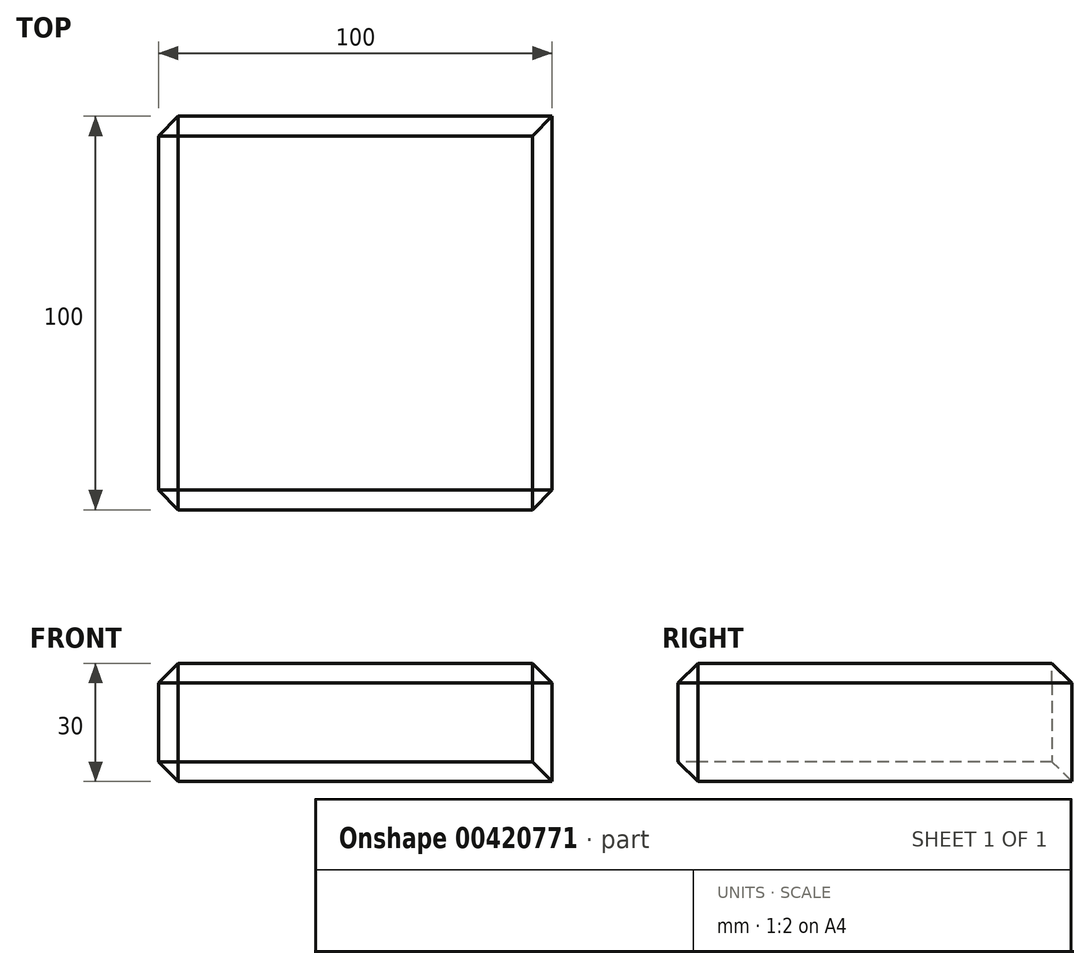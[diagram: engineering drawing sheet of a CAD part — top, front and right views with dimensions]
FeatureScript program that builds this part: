
annotation { "Feature Type Name" : "Feature", "Feature Type Description" : "" }
export const myFeature = defineFeature(function(context is Context, id is Id, definition is map)
    precondition{}
    {
        {
            var Q0;
            Q0=qCreatedBy(makeId("Top.planeOp"),FACE);
            var sketch = newSketch(context, id + "F0", { "sketchPlane" : qUnion([Q0])});
            skLineSegment(sketch, "E0.bottom", {"start": v(-34.16, 60.12) * mm, "end": v(65.84, 60.12) * mm});
            skLineSegment(sketch, "E0.top", {"start": v(-34.16, -39.88) * mm, "end": v(65.84, -39.88) * mm});
            skLineSegment(sketch, "E0.left", {"start": v(-34.16, 60.12) * mm, "end": v(-34.16, -39.88) * mm});
            skLineSegment(sketch, "E0.right", {"start": v(65.84, 60.12) * mm, "end": v(65.84, -39.88) * mm});
            skSolve(sketch);
        }
        {
            var Q0;
            Q0=makeQuery(id+"F0.imprint","IMPRINT",FACE,{"disambiguationData":[TD([[makeQuery(id+"F0.imprint","IMPRINT",EDGE,{"derivedFrom":sQuery(id+"F0.wireOp",EDGE,"E0.bottom")}),-1.0]])]});
            extrude(context, id + "F1", {"entities" : qUnion([Q0]), "depth" : 30 * mm});
        }
        {
            var Q0;
            Q0=makeQuery(id+"F1.opExtrude","CAP_FACE",FACE,{"disambiguationData":[OSD([sQuery(id+"F0.wireOp",EDGE,"E0.bottom"),sQuery(id+"F0.wireOp",EDGE,"E0.top"),sQuery(id+"F0.wireOp",EDGE,"E0.left"),sQuery(id+"F0.wireOp",EDGE,"E0.right")])],"isStart":false});
            var sketch = newSketch(context, id + "F2", { "sketchPlane" : qUnion([Q0])});
            skCircle(sketch, "E1", {"center": v(11.84, 16.56) * mm, "radius": 15 * mm});
            skSolve(sketch);
        }
        {
            var Q0;
            Q0=makeQuery(id+"F2.imprint","IMPRINT",FACE,{"disambiguationData":[TD([[makeQuery(id+"F2.imprint","IMPRINT",EDGE,{"derivedFrom":sQuery(id+"F2.wireOp",EDGE,"E1")}),-1.0]])]});
            var Q1;
            Q1=makeQuery(id+"F2.imprint","IMPRINT",FACE,{"disambiguationData":[TD([[makeQuery(id+"F2.imprint","IMPRINT",EDGE,{"derivedFrom":sQuery(id+"F2.wireOp",EDGE,"E1")}),1.0]])]});
            var Q2;
            Q2=sQuery(id+"F2.wireOp",EDGE,"E1");
            extrude(context, id + "F3", {"entities" : qUnion([Q0, Q1]), "bodyType" : ToolBodyType.SURFACE, "operationType" : NewBodyOperationType.ADD, "surfaceEntities" : qUnion([Q2]), "depth" : 40 * mm});
        }
        {
            var Q0;
            Q0=makeQuery(id+"F1.opExtrude","CAP_FACE",FACE,{"disambiguationData":[OSD([sQuery(id+"F0.wireOp",EDGE,"E0.bottom"),sQuery(id+"F0.wireOp",EDGE,"E0.top"),sQuery(id+"F0.wireOp",EDGE,"E0.left"),sQuery(id+"F0.wireOp",EDGE,"E0.right")])],"isStart":false});
            var Q1;
            Q1=makeQuery(id+"F1.opExtrude","SWEPT_FACE",FACE,{"disambiguationData":[OSD([sQuery(id+"F0.wireOp",EDGE,"E0.top")])]});
            var Q2;
            Q2=makeQuery(id+"F1.opExtrude","SWEPT_FACE",FACE,{"disambiguationData":[OSD([sQuery(id+"F0.wireOp",EDGE,"E0.left")])]});
            chamfer(context, id + "F4", {"entities" : qUnion([Q0, Q1, Q2]), "width" : 5 * mm, "tangentPropagation" : true});
        }
    });
